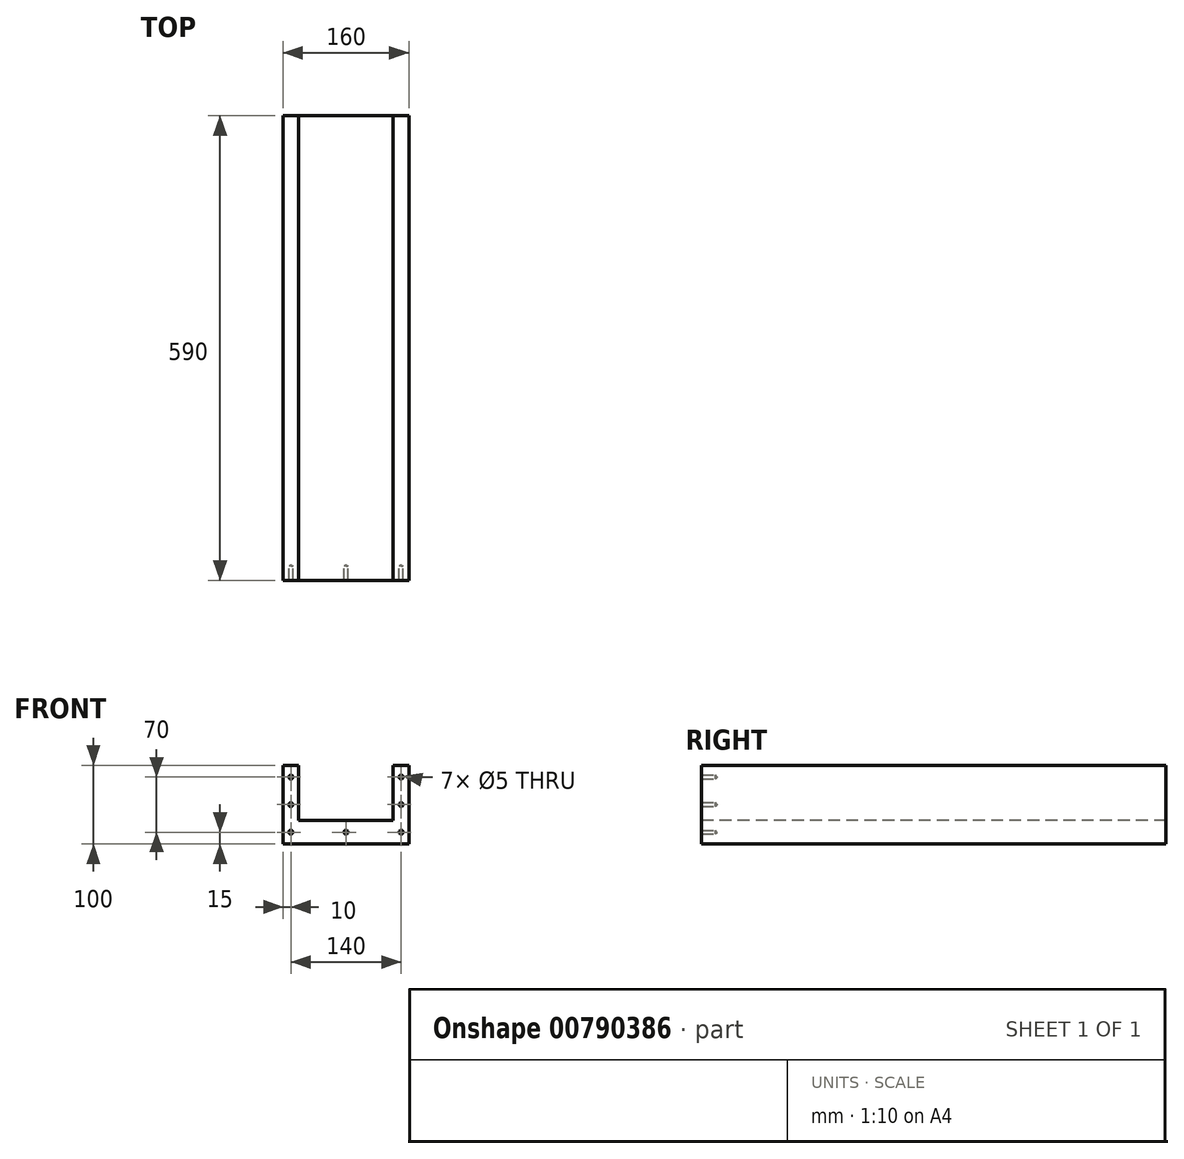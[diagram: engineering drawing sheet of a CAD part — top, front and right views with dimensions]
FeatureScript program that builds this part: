
annotation { "Feature Type Name" : "Feature", "Feature Type Description" : "" }
export const myFeature = defineFeature(function(context is Context, id is Id, definition is map)
    precondition{}
    {
        {
            var Q0;
            Q0=qCreatedBy(makeId("Front.planeOp"),FACE);
            var sketch = newSketch(context, id + "F0", { "sketchPlane" : qUnion([Q0])});
            skLineSegment(sketch, "E0.top", {"start": v(80, 70) * mm, "end": v(60, 70) * mm});
            skLineSegment(sketch, "E0.left", {"start": v(80, -30) * mm, "end": v(80, 70) * mm});
            skLineSegment(sketch, "E0.right", {"start": v(-80, -30) * mm, "end": v(-80, 70) * mm});
            skPoint(sketch, "E0.middle", {"position": v(0, 0) * mm});
            skLineSegment(sketch, "E1.trimOffspring", {"start": v(-60, 70) * mm, "end": v(-80, 70) * mm});
            skLineSegment(sketch, "E2", {"start": v(-80, -30) * mm, "end": v(80, -30) * mm});
            skPoint(sketch, "E3", {"position": v(-70, 55) * mm});
            skPoint(sketch, "E4", {"position": v(70, 55) * mm});
            skPoint(sketch, "E5", {"position": v(70, 20) * mm});
            skPoint(sketch, "E6", {"position": v(-70, 20) * mm});
            skPoint(sketch, "E7", {"position": v(-70, -15) * mm});
            skPoint(sketch, "E8", {"position": v(70, -15) * mm});
            skPoint(sketch, "E9", {"position": v(0, -15) * mm});
            skPoint(sketch, "E10", {"position": v(-70, 70) * mm});
            skPoint(sketch, "E11", {"position": v(70, 70) * mm});
            skLineSegment(sketch, "E12", {"start": v(0, 0) * mm, "end": v(60, 0) * mm});
            skLineSegment(sketch, "E13", {"start": v(60, 70) * mm, "end": v(60, 0) * mm});
            skLineSegment(sketch, "E14", {"start": v(0, 0) * mm, "end": v(-60, 0) * mm});
            skLineSegment(sketch, "E15", {"start": v(-60, 70) * mm, "end": v(-60, 0) * mm});
            skPoint(sketch, "E16.center.orphan", {"position": v(0, 70) * mm});
            skSolve(sketch);
        }
        {
            var Q0;
            Q0 = qSketchRegion(id + "F0", true);
            extrude(context, id + "F1", {"entities" : qUnion([Q0]), "oppositeDirection" : true, "depth" : 590 * mm, "offsetDistance" : 25 * mm});
        }
        {
            var Q0;
            Q0=sQuery(id+"F0.wireOp",VERTEX,"E4");
            var Q1;
            Q1=sQuery(id+"F0.wireOp",VERTEX,"E5");
            var Q2;
            Q2=sQuery(id+"F0.wireOp",VERTEX,"E8");
            var Q3;
            Q3=sQuery(id+"F0.wireOp",VERTEX,"E9");
            var Q4;
            Q4=sQuery(id+"F0.wireOp",VERTEX,"E7");
            var Q5;
            Q5=sQuery(id+"F0.wireOp",VERTEX,"E6");
            var Q6;
            Q6=sQuery(id+"F0.wireOp",VERTEX,"E3");
            var Q7;
            Q7=makeQuery(id+"F1.opExtrude","SWEPT_BODY",BODY,{"disambiguationData":[OSD([sQuery(id+"F0.wireOp",EDGE,"E0.top"),sQuery(id+"F0.wireOp",EDGE,"E0.left"),sQuery(id+"F0.wireOp",EDGE,"E0.right"),sQuery(id+"F0.wireOp",EDGE,"E1.trimOffspring"),sQuery(id+"F0.wireOp",EDGE,"E2"),sQuery(id+"F0.wireOp",EDGE,"E12"),sQuery(id+"F0.wireOp",EDGE,"E13"),sQuery(id+"F0.wireOp",EDGE,"E14"),sQuery(id+"F0.wireOp",EDGE,"E15")])]});
            hole(context, id + "F2", {"style" : HoleStyle.SIMPLE, "endStyle" : HoleEndStyle.BLIND, "standardTappedOrClearance" : lookupTablePath({ "standard" : "ISO", "engagement" : "75%", "pitch" : "1 mm", "size" : "M6", "type" : "Tapped" }), "standardBlindInLast" : lookupTablePath({ "standard" : "ISO", "engagement" : "75%", "pitch" : "1 mm", "size" : "M6", "type" : "Tapped" }), "holeDiameter" : 5 * mm, "majorDiameter" : 6 * mm, "showTappedDepth" : true, "holeDepth" : 18 * mm, "isTappedThrough" : true, "tappedDepth" : 15 * mm, "tapClearance" : 3, "startFromSketch" : true, "locations" : qUnion([Q0, Q1, Q2, Q3, Q4, Q5, Q6]), "scope" : qUnion([Q7])});
        }
        {
            var Q0;
            Q0=makeQuery(id+"F0.imprint","IMPRINT",FACE,{"disambiguationData":[TD([[makeQuery(id+"F0.imprint","IMPRINT",EDGE,{"derivedFrom":sQuery(id+"F0.wireOp",EDGE,"E0.top")}),1.0]])]});
            cPlane(context, id + "F3", {"entities" : qUnion([Q0]), "cplaneType" : CPlaneType.OFFSET, "offset" : 295 * mm, "oppositeDirection" : true, "width" : 150 * mm, "height" : 150 * mm});
        }
    });
